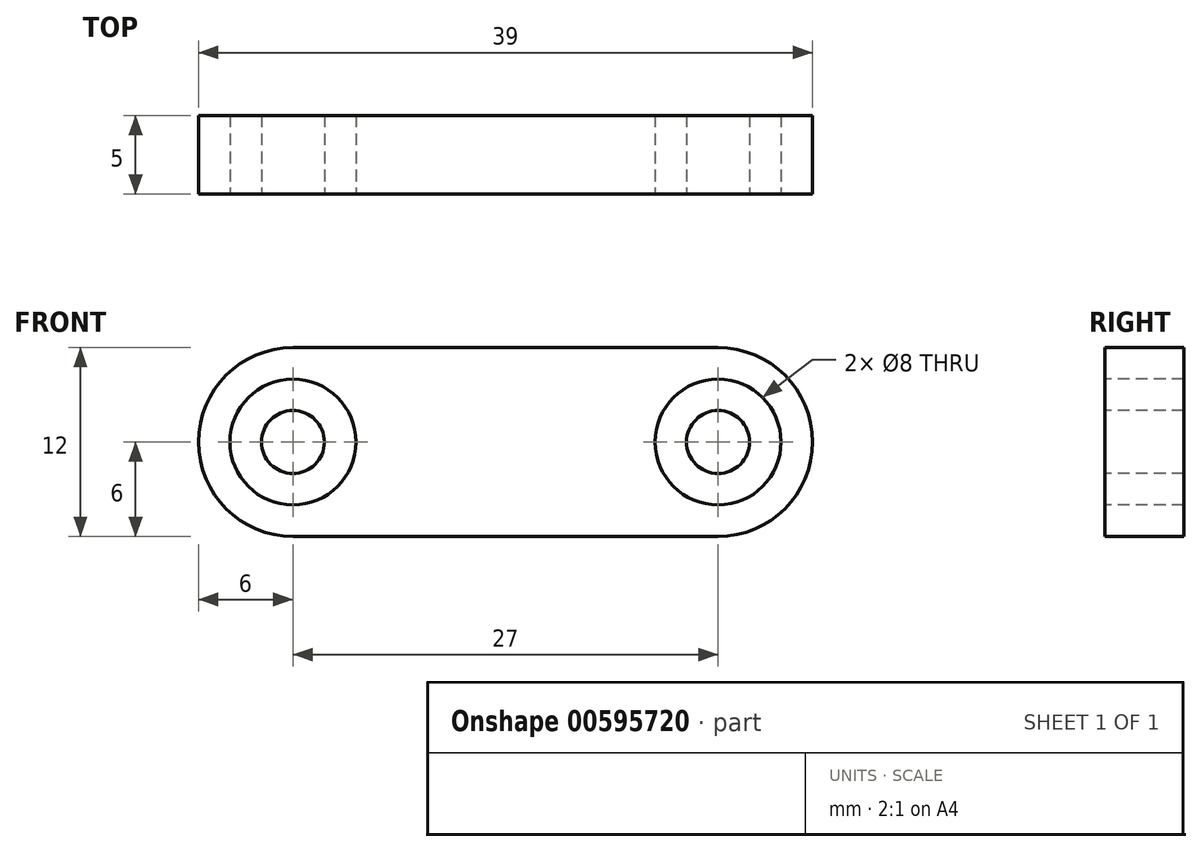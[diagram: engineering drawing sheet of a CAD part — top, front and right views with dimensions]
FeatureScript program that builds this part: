
annotation { "Feature Type Name" : "Feature", "Feature Type Description" : "" }
export const myFeature = defineFeature(function(context is Context, id is Id, definition is map)
    precondition{}
    {
        {
            var Q0;
            Q0=qCreatedBy(makeId("Front.planeOp"),FACE);
            var sketch = newSketch(context, id + "F0", { "sketchPlane" : qUnion([Q0])});
            skCircle(sketch, "E0", {"center": v(-15, 0) * mm, "radius": 6 * mm});
            skCircle(sketch, "E1", {"center": v(12, 0) * mm, "radius": 6 * mm});
            skLineSegment(sketch, "E2", {"start": v(-15, 6) * mm, "end": v(12, 6) * mm});
            skLineSegment(sketch, "E3", {"start": v(-15, -6) * mm, "end": v(12, -6) * mm});
            skSolve(sketch);
        }
        {
            var Q0;
            Q0 = qSketchRegion(id + "F0", true);
            extrude(context, id + "F1", {"entities" : qUnion([Q0]), "depth" : 5 * mm, "offsetDistance" : 25 * mm});
        }
        {
            var Q0;
            Q0=makeQuery(id+"F1.opExtrude","CAP_FACE",FACE,{"disambiguationData":[OSD([sQuery(id+"F0.wireOp",EDGE,"E0"),sQuery(id+"F0.wireOp",EDGE,"E1"),sQuery(id+"F0.wireOp",EDGE,"E2"),sQuery(id+"F0.wireOp",EDGE,"E3")])],"isStart":false});
            var sketch = newSketch(context, id + "F2", { "sketchPlane" : qUnion([Q0])});
            skCircle(sketch, "E4", {"center": v(-15, 0) * mm, "radius": 4 * mm});
            skCircle(sketch, "E5", {"center": v(12, 0) * mm, "radius": 4 * mm});
            skCircle(sketch, "E6", {"center": v(12, 0) * mm, "radius": 2 * mm});
            skCircle(sketch, "E7", {"center": v(-15, 0) * mm, "radius": 2 * mm});
            skSolve(sketch);
        }
        {
            var Q0;
            Q0 = qSketchRegion(id + "F2", true);
            extrude(context, id + "F3", {"entities" : qUnion([Q0]), "operationType" : NewBodyOperationType.REMOVE, "oppositeDirection" : true, "depth" : 25 * mm, "offsetDistance" : 25 * mm});
        }
    });
